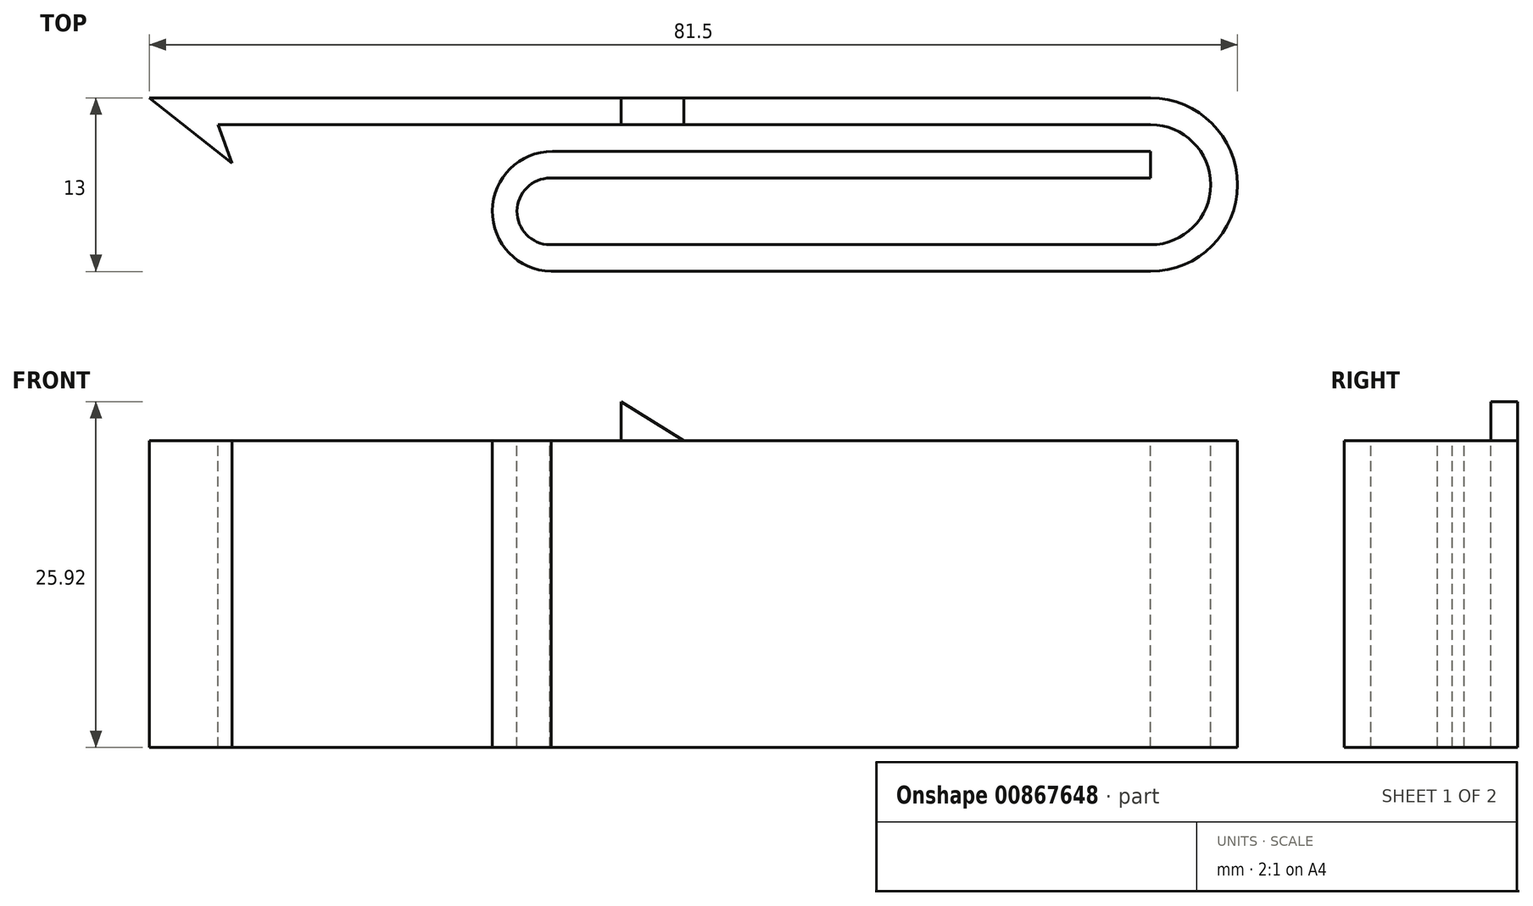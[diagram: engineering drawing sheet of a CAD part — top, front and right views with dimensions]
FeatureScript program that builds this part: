
annotation { "Feature Type Name" : "Feature", "Feature Type Description" : "" }
export const myFeature = defineFeature(function(context is Context, id is Id, definition is map)
    precondition{}
    {
        {
            var Q0;
            Q0=qCreatedBy(makeId("Top.planeOp"),FACE);
            var sketch = newSketch(context, id + "F0", { "sketchPlane" : qUnion([Q0])});
            skLineSegment(sketch, "E0", {"start": v(-35.22, 4.42) * mm, "end": v(34.65, 4.42) * mm});
            skLineSegment(sketch, "E1", {"start": v(34.65, -4.58) * mm, "end": v(-10.35, -4.58) * mm});
            skArc(sketch, "E2", {"start": v(34.65, -4.58) * mm, "mid": v(39.15, -0.08) * mm, "end": v(34.65, 4.42) * mm});
            skLineSegment(sketch, "E3.0", {"start": v(34.65, -6.58) * mm, "end": v(-10.27, -6.58) * mm});
            skArc(sketch, "E3.1", {"start": v(34.65, -6.58) * mm, "mid": v(41.15, -0.08) * mm, "end": v(34.65, 6.42) * mm});
            skLineSegment(sketch, "E3.2", {"start": v(-40.35, 6.42) * mm, "end": v(34.65, 6.42) * mm});
            skLineSegment(sketch, "E4", {"start": v(-35.22, 4.42) * mm, "end": v(-34.16, 1.53) * mm});
            skLineSegment(sketch, "E5", {"start": v(-34.16, 1.53) * mm, "end": v(-40.35, 6.42) * mm});
            skLineSegment(sketch, "E6.0", {"start": v(34.66, 0.42) * mm, "end": v(-10.31, 0.42) * mm});
            skLineSegment(sketch, "E7.0", {"start": v(34.66, 2.42) * mm, "end": v(-10.16, 2.42) * mm});
            skLineSegment(sketch, "E8", {"start": v(34.66, 0.42) * mm, "end": v(34.66, 2.42) * mm});
            skArc(sketch, "E9", {"start": v(-10.31, 0.42) * mm, "mid": v(-12.81, -2.06) * mm, "end": v(-10.35, -4.58) * mm});
            skArc(sketch, "E10", {"start": v(-10.16, 2.42) * mm, "mid": v(-14.66, -2.03) * mm, "end": v(-10.27, -6.58) * mm});
            skSolve(sketch);
        }
        {
            var Q0;
            Q0 = qSketchRegion(id + "F0", true);
            extrude(context, id + "F1", {"entities" : qUnion([Q0]), "oppositeDirection" : true, "depth" : 23 * mm, "offsetDistance" : 25 * mm});
        }
        {
            var Q0;
            Q0=makeQuery(id+"F1.opExtrude","SWEPT_FACE",FACE,{"disambiguationData":[OSD([sQuery(id+"F0.wireOp",EDGE,"E3.2")])]});
            var sketch = newSketch(context, id + "F2", { "sketchPlane" : qUnion([Q0])});
            skLineSegment(sketch, "E11", {"start": v(5.03, -1.14) * mm, "end": v(5.03, 2.92) * mm});
            skLineSegment(sketch, "E12", {"start": v(5.03, 2.92) * mm, "end": v(-1.52, -1.14) * mm});
            skLineSegment(sketch, "E13", {"start": v(-1.52, -1.14) * mm, "end": v(5.03, -1.14) * mm});
            skSolve(sketch);
        }
        {
            var Q0;
            {var subQ0=sQuery(id+"F2.wireOp",EDGE,"E12");var subQ1=sQuery(id+"F2.wireOp",EDGE,"E11");var subQ2=makeQuery(id+"F2.imprint","INTERSECT",VERTEX,{"derivedFrom":[subQ1,subQ0]});Q0=makeQuery(id+"F2.imprint","IMPRINT",FACE,{"disambiguationData":[TD([[makeQuery(id+"F2.imprint","IMPRINT",EDGE,{"disambiguationData":[TD([[subQ2,1.0]])],"derivedFrom":subQ1}),1.0]])]});}
            extrude(context, id + "F3", {"entities" : qUnion([Q0]), "oppositeDirection" : true, "depth" : 2 * mm, "offsetDistance" : 25 * mm});
        }
    });
